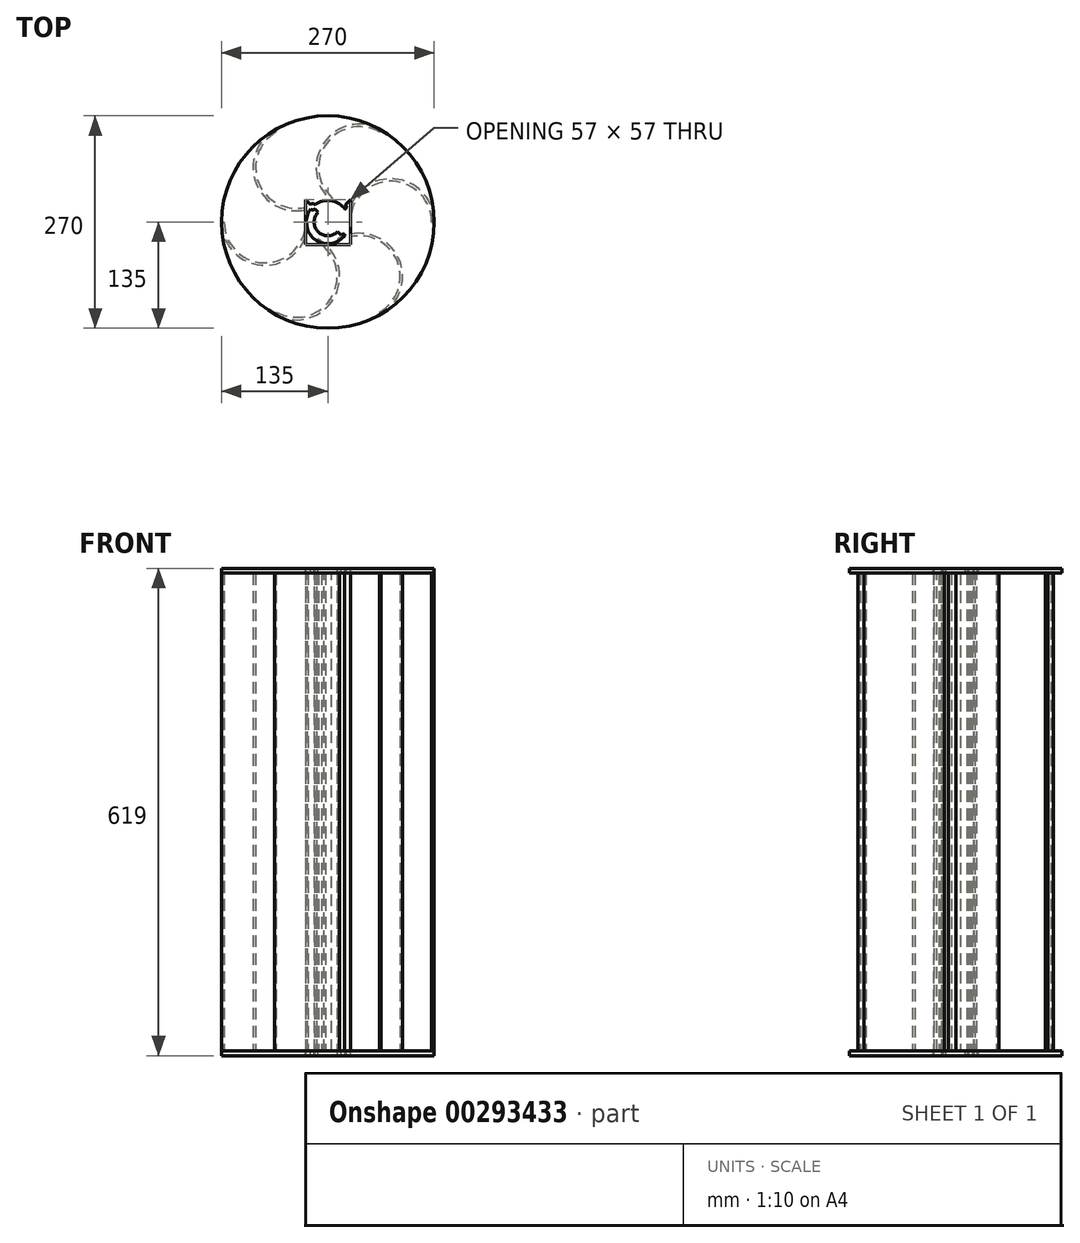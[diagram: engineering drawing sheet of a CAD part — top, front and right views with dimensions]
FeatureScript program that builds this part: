
annotation { "Feature Type Name" : "Feature", "Feature Type Description" : "" }
export const myFeature = defineFeature(function(context is Context, id is Id, definition is map)
    precondition{}
    {
        {
            var Q0;
            Q0=qCreatedBy(makeId("Top.planeOp"),FACE);
            var sketch = newSketch(context, id + "F0", { "sketchPlane" : qUnion([Q0])});
            skCircle(sketch, "E0", {"center": v(0, 0) * mm, "radius": 135 * mm});
            skSolve(sketch);
        }
        {
            var Q0;
            Q0 = qSketchRegion(id + "F0", true);
            extrude(context, id + "F1", {"entities" : qUnion([Q0]), "depth" : 6 * mm});
        }
        {
            var Q0;
            Q0=makeQuery(id+"F1.opExtrude","CAP_FACE",FACE,{"disambiguationData":[OSD([sQuery(id+"F0.wireOp",EDGE,"E0")])],"isStart":false});
            var sketch = newSketch(context, id + "F2", { "sketchPlane" : qUnion([Q0])});
            skCircle(sketch, "E1", {"center": v(0, 0) * mm, "radius": 80 * mm});
            skLineSegment(sketch, "E2", {"start": v(-67.5, 116.91) * mm, "end": v(67.5, -116.91) * mm});
            skLineSegment(sketch, "E3", {"start": v(-67.5, -116.91) * mm, "end": v(67.5, 116.91) * mm});
            skLineSegment(sketch, "E4", {"start": v(-135, 0) * mm, "end": v(135, 0) * mm});
            skArc(sketch, "E5", {"start": v(-131.8, 0) * mm, "mid": v(-80, -51.8) * mm, "end": v(-28.2, 0) * mm});
            skArc(sketch, "E6", {"start": v(-65.9, -114.14) * mm, "mid": v(4.86, -95.18) * mm, "end": v(-14.1, -24.42) * mm});
            skArc(sketch, "E7", {"start": v(65.9, -114.14) * mm, "mid": v(84.86, -43.38) * mm, "end": v(14.1, -24.42) * mm});
            skArc(sketch, "E8", {"start": v(131.8, 0) * mm, "mid": v(80, 51.8) * mm, "end": v(28.2, 0) * mm});
            skArc(sketch, "E9", {"start": v(65.9, 114.14) * mm, "mid": v(-4.86, 95.18) * mm, "end": v(14.1, 24.42) * mm});
            skArc(sketch, "E10", {"start": v(-65.9, 114.14) * mm, "mid": v(-84.86, 43.38) * mm, "end": v(-14.1, 24.42) * mm});
            skArc(sketch, "E11.0", {"start": v(-67.5, 116.91) * mm, "mid": v(-87.63, 41.78) * mm, "end": v(-12.5, 21.65) * mm});
            skArc(sketch, "E12.0", {"start": v(-135, 0) * mm, "mid": v(-80, -55) * mm, "end": v(-25, 0) * mm});
            skArc(sketch, "E13.0", {"start": v(-67.5, -116.91) * mm, "mid": v(7.63, -96.78) * mm, "end": v(-12.5, -21.65) * mm});
            skArc(sketch, "E14.0", {"start": v(67.5, -116.91) * mm, "mid": v(87.63, -41.78) * mm, "end": v(12.5, -21.65) * mm});
            skArc(sketch, "E15.0", {"start": v(135, 0) * mm, "mid": v(80, 55) * mm, "end": v(25, 0) * mm});
            skArc(sketch, "E16.0", {"start": v(67.5, 116.91) * mm, "mid": v(-7.63, 96.78) * mm, "end": v(12.5, 21.65) * mm});
            skSolve(sketch);
        }
        {
            var Q0;
            {var subQ0=sQuery(id+"F2.wireOp",EDGE,"E5");var subQ1=sQuery(id+"F2.wireOp",EDGE,"E1");var subQ2=makeQuery(id+"F2.imprint","INTERSECT",VERTEX,{"derivedFrom":[subQ1,subQ0]});Q0=makeQuery(id+"F2.imprint","IMPRINT",FACE,{"disambiguationData":[TD([[makeQuery(id+"F2.imprint","IMPRINT",EDGE,{"disambiguationData":[TD([[subQ2,-1.0]])],"derivedFrom":subQ1}),-1.0]])]});}
            var Q1;
            {var subQ0=sQuery(id+"F2.wireOp",EDGE,"E5");var subQ1=sQuery(id+"F2.wireOp",EDGE,"E1");var subQ2=makeQuery(id+"F2.imprint","INTERSECT",VERTEX,{"derivedFrom":[subQ1,subQ0]});Q1=makeQuery(id+"F2.imprint","IMPRINT",FACE,{"disambiguationData":[TD([[makeQuery(id+"F2.imprint","IMPRINT",EDGE,{"disambiguationData":[TD([[subQ2,-1.0]])],"derivedFrom":subQ1}),1.0]])]});}
            var Q2;
            {var subQ0=sQuery(id+"F2.wireOp",EDGE,"E6");var subQ1=sQuery(id+"F2.wireOp",EDGE,"E1");var subQ2=makeQuery(id+"F2.imprint","INTERSECT",VERTEX,{"derivedFrom":[subQ1,subQ0]});Q2=makeQuery(id+"F2.imprint","IMPRINT",FACE,{"disambiguationData":[TD([[makeQuery(id+"F2.imprint","IMPRINT",EDGE,{"disambiguationData":[TD([[subQ2,-1.0]])],"derivedFrom":subQ1}),1.0]])]});}
            var Q3;
            {var subQ0=sQuery(id+"F2.wireOp",EDGE,"E6");var subQ1=sQuery(id+"F2.wireOp",EDGE,"E1");var subQ2=makeQuery(id+"F2.imprint","INTERSECT",VERTEX,{"derivedFrom":[subQ1,subQ0]});Q3=makeQuery(id+"F2.imprint","IMPRINT",FACE,{"disambiguationData":[TD([[makeQuery(id+"F2.imprint","IMPRINT",EDGE,{"disambiguationData":[TD([[subQ2,-1.0]])],"derivedFrom":subQ1}),-1.0]])]});}
            var Q4;
            {var subQ0=sQuery(id+"F2.wireOp",EDGE,"E10");var subQ1=sQuery(id+"F2.wireOp",EDGE,"E1");var subQ2=makeQuery(id+"F2.imprint","INTERSECT",VERTEX,{"derivedFrom":[subQ1,subQ0]});Q4=makeQuery(id+"F2.imprint","IMPRINT",FACE,{"disambiguationData":[TD([[makeQuery(id+"F2.imprint","IMPRINT",EDGE,{"disambiguationData":[TD([[subQ2,-1.0]])],"derivedFrom":subQ1}),1.0]])]});}
            var Q5;
            {var subQ0=sQuery(id+"F2.wireOp",EDGE,"E10");var subQ1=sQuery(id+"F2.wireOp",EDGE,"E1");var subQ2=makeQuery(id+"F2.imprint","INTERSECT",VERTEX,{"derivedFrom":[subQ1,subQ0]});Q5=makeQuery(id+"F2.imprint","IMPRINT",FACE,{"disambiguationData":[TD([[makeQuery(id+"F2.imprint","IMPRINT",EDGE,{"disambiguationData":[TD([[subQ2,-1.0]])],"derivedFrom":subQ1}),-1.0]])]});}
            var Q6;
            {var subQ0=sQuery(id+"F2.wireOp",EDGE,"E9");var subQ1=sQuery(id+"F2.wireOp",EDGE,"E1");var subQ2=makeQuery(id+"F2.imprint","INTERSECT",VERTEX,{"derivedFrom":[subQ1,subQ0]});Q6=makeQuery(id+"F2.imprint","IMPRINT",FACE,{"disambiguationData":[TD([[makeQuery(id+"F2.imprint","IMPRINT",EDGE,{"disambiguationData":[TD([[subQ2,-1.0]])],"derivedFrom":subQ1}),-1.0]])]});}
            var Q7;
            {var subQ0=sQuery(id+"F2.wireOp",EDGE,"E9");var subQ1=sQuery(id+"F2.wireOp",EDGE,"E1");var subQ2=makeQuery(id+"F2.imprint","INTERSECT",VERTEX,{"derivedFrom":[subQ1,subQ0]});Q7=makeQuery(id+"F2.imprint","IMPRINT",FACE,{"disambiguationData":[TD([[makeQuery(id+"F2.imprint","IMPRINT",EDGE,{"disambiguationData":[TD([[subQ2,-1.0]])],"derivedFrom":subQ1}),1.0]])]});}
            var Q8;
            {var subQ0=sQuery(id+"F2.wireOp",EDGE,"E8");var subQ1=sQuery(id+"F2.wireOp",EDGE,"E1");var subQ2=makeQuery(id+"F2.imprint","INTERSECT",VERTEX,{"derivedFrom":[subQ1,subQ0]});Q8=makeQuery(id+"F2.imprint","IMPRINT",FACE,{"disambiguationData":[TD([[makeQuery(id+"F2.imprint","IMPRINT",EDGE,{"disambiguationData":[TD([[subQ2,-1.0]])],"derivedFrom":subQ1}),1.0]])]});}
            var Q9;
            {var subQ0=sQuery(id+"F2.wireOp",EDGE,"E7");var subQ1=sQuery(id+"F2.wireOp",EDGE,"E1");var subQ2=makeQuery(id+"F2.imprint","INTERSECT",VERTEX,{"derivedFrom":[subQ1,subQ0]});Q9=makeQuery(id+"F2.imprint","IMPRINT",FACE,{"disambiguationData":[TD([[makeQuery(id+"F2.imprint","IMPRINT",EDGE,{"disambiguationData":[TD([[subQ2,-1.0]])],"derivedFrom":subQ1}),1.0]])]});}
            var Q10;
            {var subQ0=sQuery(id+"F2.wireOp",EDGE,"E7");var subQ1=sQuery(id+"F2.wireOp",EDGE,"E1");var subQ2=makeQuery(id+"F2.imprint","INTERSECT",VERTEX,{"derivedFrom":[subQ1,subQ0]});Q10=makeQuery(id+"F2.imprint","IMPRINT",FACE,{"disambiguationData":[TD([[makeQuery(id+"F2.imprint","IMPRINT",EDGE,{"disambiguationData":[TD([[subQ2,-1.0]])],"derivedFrom":subQ1}),-1.0]])]});}
            var Q11;
            {var subQ0=sQuery(id+"F2.wireOp",EDGE,"E8");var subQ1=sQuery(id+"F2.wireOp",EDGE,"E1");var subQ2=makeQuery(id+"F2.imprint","INTERSECT",VERTEX,{"derivedFrom":[subQ1,subQ0]});Q11=makeQuery(id+"F2.imprint","IMPRINT",FACE,{"disambiguationData":[TD([[makeQuery(id+"F2.imprint","IMPRINT",EDGE,{"disambiguationData":[TD([[subQ2,-1.0]])],"derivedFrom":subQ1}),-1.0]])]});}
            extrude(context, id + "F3", {"entities" : qUnion([Q0, Q1, Q2, Q3, Q4, Q5, Q6, Q7, Q8, Q9, Q10, Q11]), "operationType" : NewBodyOperationType.ADD, "depth" : 607 * mm, "offsetDistance" : 25 * mm});
        }
        {
            var Q0;
            Q0=makeQuery(id+"F3.opExtrude","CAP_FACE",FACE,{"disambiguationData":[OSD([sQuery(id+"F2.wireOp",EDGE,"E2"),sQuery(id+"F2.wireOp",EDGE,"E10"),sQuery(id+"F2.wireOp",EDGE,"E11.0")])],"isStart":false});
            var sketch = newSketch(context, id + "F4", { "sketchPlane" : qUnion([Q0])});
            skCircle(sketch, "E17", {"center": v(0, 0) * mm, "radius": 135 * mm});
            skSolve(sketch);
        }
        {
            var Q0;
            Q0 = qSketchRegion(id + "F4", true);
            extrude(context, id + "F5", {"entities" : qUnion([Q0]), "operationType" : NewBodyOperationType.ADD, "depth" : 6 * mm});
        }
        {
            var Q0;
            Q0=makeQuery(id+"F5.opExtrude","CAP_FACE",FACE,{"disambiguationData":[OSD([sQuery(id+"F4.wireOp",EDGE,"E17")])],"isStart":false});
            var sketch = newSketch(context, id + "F6", { "sketchPlane" : qUnion([Q0])});
            skCircle(sketch, "E18", {"center": v(0, 0) * mm, "radius": 17.5 * mm});
            skLineSegment(sketch, "E19.bottom", {"start": v(28.5, 28.5) * mm, "end": v(-28.5, 28.5) * mm});
            skLineSegment(sketch, "E19.top", {"start": v(28.5, -28.5) * mm, "end": v(-28.5, -28.5) * mm});
            skLineSegment(sketch, "E19.left", {"start": v(28.5, 28.5) * mm, "end": v(28.5, -28.5) * mm});
            skLineSegment(sketch, "E19.right", {"start": v(-28.5, 28.5) * mm, "end": v(-28.5, -28.5) * mm});
            skLineSegment(sketch, "E20", {"start": v(-28.5, 28.5) * mm, "end": v(28.5, -28.5) * mm});
            skLineSegment(sketch, "E21", {"start": v(28.5, 28.5) * mm, "end": v(-28.5, -28.5) * mm});
            skCircle(sketch, "E22", {"center": v(0, 0) * mm, "radius": 27.5 * mm});
            skCircle(sketch, "E23", {"center": v(-19.45, 19.45) * mm, "radius": 4 * mm});
            skCircle(sketch, "E24", {"center": v(-19.45, -19.45) * mm, "radius": 4 * mm});
            skCircle(sketch, "E25", {"center": v(19.45, -19.45) * mm, "radius": 4 * mm});
            skCircle(sketch, "E26", {"center": v(19.45, 19.45) * mm, "radius": 4 * mm});
            skSolve(sketch);
        }
        {
            var Q0;
            {var subQ0=sQuery(id+"F6.wireOp",EDGE,"E23");var subQ1=sQuery(id+"F6.wireOp",EDGE,"E20");var subQ2=makeQuery(id+"F6.imprint","INTERSECT",VERTEX,{"disambiguationData":[OD(0.0)],"derivedFrom":[subQ1,subQ0]});Q0=makeQuery(id+"F6.imprint","IMPRINT",FACE,{"disambiguationData":[TD([[makeQuery(id+"F6.imprint","IMPRINT",EDGE,{"disambiguationData":[TD([[subQ2,-1.0]])],"derivedFrom":subQ1}),1.0]])]});}
            var Q1;
            {var subQ0=sQuery(id+"F6.wireOp",EDGE,"E23");var subQ1=sQuery(id+"F6.wireOp",EDGE,"E20");var subQ2=makeQuery(id+"F6.imprint","INTERSECT",VERTEX,{"disambiguationData":[OD(0.0)],"derivedFrom":[subQ1,subQ0]});Q1=makeQuery(id+"F6.imprint","IMPRINT",FACE,{"disambiguationData":[TD([[makeQuery(id+"F6.imprint","IMPRINT",EDGE,{"disambiguationData":[TD([[subQ2,-1.0]])],"derivedFrom":subQ1}),-1.0]])]});}
            var Q2;
            {var subQ0=sQuery(id+"F6.wireOp",EDGE,"E22");var subQ1=sQuery(id+"F6.wireOp",EDGE,"E20");var subQ2=makeQuery(id+"F6.imprint","INTERSECT",VERTEX,{"disambiguationData":[OD(0.0)],"derivedFrom":[subQ1,subQ0]});Q2=makeQuery(id+"F6.imprint","IMPRINT",FACE,{"disambiguationData":[TD([[makeQuery(id+"F6.imprint","IMPRINT",EDGE,{"disambiguationData":[TD([[subQ2,-1.0]])],"derivedFrom":subQ1}),-1.0]])]});}
            var Q3;
            {var subQ0=sQuery(id+"F6.wireOp",EDGE,"E22");var subQ1=sQuery(id+"F6.wireOp",EDGE,"E20");var subQ2=makeQuery(id+"F6.imprint","INTERSECT",VERTEX,{"disambiguationData":[OD(0.0)],"derivedFrom":[subQ1,subQ0]});Q3=makeQuery(id+"F6.imprint","IMPRINT",FACE,{"disambiguationData":[TD([[makeQuery(id+"F6.imprint","IMPRINT",EDGE,{"disambiguationData":[TD([[subQ2,-1.0]])],"derivedFrom":subQ1}),1.0]])]});}
            var Q4;
            {var subQ0=sQuery(id+"F6.wireOp",EDGE,"E20");var subQ1=sQuery(id+"F6.wireOp",EDGE,"E18");var subQ2=makeQuery(id+"F6.imprint","INTERSECT",VERTEX,{"disambiguationData":[OD(0.0)],"derivedFrom":[subQ1,subQ0]});Q4=makeQuery(id+"F6.imprint","IMPRINT",FACE,{"disambiguationData":[TD([[makeQuery(id+"F6.imprint","IMPRINT",EDGE,{"disambiguationData":[TD([[subQ2,-1.0]])],"derivedFrom":subQ1}),1.0]])]});}
            var Q5;
            {var subQ0=sQuery(id+"F6.wireOp",EDGE,"E21");var subQ1=sQuery(id+"F6.wireOp",EDGE,"E18");var subQ2=makeQuery(id+"F6.imprint","INTERSECT",VERTEX,{"disambiguationData":[OD(1.0)],"derivedFrom":[subQ1,subQ0]});Q5=makeQuery(id+"F6.imprint","IMPRINT",FACE,{"disambiguationData":[TD([[makeQuery(id+"F6.imprint","IMPRINT",EDGE,{"disambiguationData":[TD([[subQ2,-1.0]])],"derivedFrom":subQ1}),1.0]])]});}
            var Q6;
            {var subQ0=sQuery(id+"F6.wireOp",EDGE,"E21");var subQ1=sQuery(id+"F6.wireOp",EDGE,"E18");var subQ2=makeQuery(id+"F6.imprint","INTERSECT",VERTEX,{"disambiguationData":[OD(0.0)],"derivedFrom":[subQ1,subQ0]});Q6=makeQuery(id+"F6.imprint","IMPRINT",FACE,{"disambiguationData":[TD([[makeQuery(id+"F6.imprint","IMPRINT",EDGE,{"disambiguationData":[TD([[subQ2,1.0]])],"derivedFrom":subQ1}),1.0]])]});}
            var Q7;
            {var subQ0=sQuery(id+"F6.wireOp",EDGE,"E20");var subQ1=sQuery(id+"F6.wireOp",EDGE,"E18");var subQ2=makeQuery(id+"F6.imprint","INTERSECT",VERTEX,{"disambiguationData":[OD(0.0)],"derivedFrom":[subQ1,subQ0]});Q7=makeQuery(id+"F6.imprint","IMPRINT",FACE,{"disambiguationData":[TD([[makeQuery(id+"F6.imprint","IMPRINT",EDGE,{"disambiguationData":[TD([[subQ2,1.0]])],"derivedFrom":subQ1}),1.0]])]});}
            var Q8;
            {var subQ0=sQuery(id+"F6.wireOp",EDGE,"E26");var subQ1=sQuery(id+"F6.wireOp",EDGE,"E21");var subQ2=makeQuery(id+"F6.imprint","INTERSECT",VERTEX,{"disambiguationData":[OD(0.0)],"derivedFrom":[subQ1,subQ0]});Q8=makeQuery(id+"F6.imprint","IMPRINT",FACE,{"disambiguationData":[TD([[makeQuery(id+"F6.imprint","IMPRINT",EDGE,{"disambiguationData":[TD([[subQ2,-1.0]])],"derivedFrom":subQ1}),1.0]])]});}
            var Q9;
            {var subQ0=sQuery(id+"F6.wireOp",EDGE,"E26");var subQ1=sQuery(id+"F6.wireOp",EDGE,"E21");var subQ2=makeQuery(id+"F6.imprint","INTERSECT",VERTEX,{"disambiguationData":[OD(0.0)],"derivedFrom":[subQ1,subQ0]});Q9=makeQuery(id+"F6.imprint","IMPRINT",FACE,{"disambiguationData":[TD([[makeQuery(id+"F6.imprint","IMPRINT",EDGE,{"disambiguationData":[TD([[subQ2,-1.0]])],"derivedFrom":subQ1}),-1.0]])]});}
            var Q10;
            {var subQ0=sQuery(id+"F6.wireOp",EDGE,"E22");var subQ1=sQuery(id+"F6.wireOp",EDGE,"E21");var subQ2=makeQuery(id+"F6.imprint","INTERSECT",VERTEX,{"disambiguationData":[OD(0.0)],"derivedFrom":[subQ1,subQ0]});Q10=makeQuery(id+"F6.imprint","IMPRINT",FACE,{"disambiguationData":[TD([[makeQuery(id+"F6.imprint","IMPRINT",EDGE,{"disambiguationData":[TD([[subQ2,-1.0]])],"derivedFrom":subQ1}),-1.0]])]});}
            var Q11;
            {var subQ0=sQuery(id+"F6.wireOp",EDGE,"E22");var subQ1=sQuery(id+"F6.wireOp",EDGE,"E21");var subQ2=makeQuery(id+"F6.imprint","INTERSECT",VERTEX,{"disambiguationData":[OD(0.0)],"derivedFrom":[subQ1,subQ0]});Q11=makeQuery(id+"F6.imprint","IMPRINT",FACE,{"disambiguationData":[TD([[makeQuery(id+"F6.imprint","IMPRINT",EDGE,{"disambiguationData":[TD([[subQ2,-1.0]])],"derivedFrom":subQ1}),1.0]])]});}
            var Q12;
            {var subQ0=sQuery(id+"F6.wireOp",EDGE,"E22");var subQ1=sQuery(id+"F6.wireOp",EDGE,"E20");var subQ2=makeQuery(id+"F6.imprint","INTERSECT",VERTEX,{"disambiguationData":[OD(1.0)],"derivedFrom":[subQ1,subQ0]});Q12=makeQuery(id+"F6.imprint","IMPRINT",FACE,{"disambiguationData":[TD([[makeQuery(id+"F6.imprint","IMPRINT",EDGE,{"disambiguationData":[TD([[subQ2,-1.0]])],"derivedFrom":subQ1}),-1.0]])]});}
            var Q13;
            {var subQ0=sQuery(id+"F6.wireOp",EDGE,"E22");var subQ1=sQuery(id+"F6.wireOp",EDGE,"E20");var subQ2=makeQuery(id+"F6.imprint","INTERSECT",VERTEX,{"disambiguationData":[OD(1.0)],"derivedFrom":[subQ1,subQ0]});Q13=makeQuery(id+"F6.imprint","IMPRINT",FACE,{"disambiguationData":[TD([[makeQuery(id+"F6.imprint","IMPRINT",EDGE,{"disambiguationData":[TD([[subQ2,-1.0]])],"derivedFrom":subQ1}),1.0]])]});}
            var Q14;
            {var subQ0=sQuery(id+"F6.wireOp",EDGE,"E25");var subQ1=sQuery(id+"F6.wireOp",EDGE,"E20");var subQ2=makeQuery(id+"F6.imprint","INTERSECT",VERTEX,{"disambiguationData":[OD(0.0)],"derivedFrom":[subQ1,subQ0]});Q14=makeQuery(id+"F6.imprint","IMPRINT",FACE,{"disambiguationData":[TD([[makeQuery(id+"F6.imprint","IMPRINT",EDGE,{"disambiguationData":[TD([[subQ2,-1.0]])],"derivedFrom":subQ1}),1.0]])]});}
            var Q15;
            {var subQ0=sQuery(id+"F6.wireOp",EDGE,"E25");var subQ1=sQuery(id+"F6.wireOp",EDGE,"E20");var subQ2=makeQuery(id+"F6.imprint","INTERSECT",VERTEX,{"disambiguationData":[OD(0.0)],"derivedFrom":[subQ1,subQ0]});Q15=makeQuery(id+"F6.imprint","IMPRINT",FACE,{"disambiguationData":[TD([[makeQuery(id+"F6.imprint","IMPRINT",EDGE,{"disambiguationData":[TD([[subQ2,-1.0]])],"derivedFrom":subQ1}),-1.0]])]});}
            var Q16;
            {var subQ0=sQuery(id+"F6.wireOp",EDGE,"E22");var subQ1=sQuery(id+"F6.wireOp",EDGE,"E21");var subQ2=makeQuery(id+"F6.imprint","INTERSECT",VERTEX,{"disambiguationData":[OD(1.0)],"derivedFrom":[subQ1,subQ0]});Q16=makeQuery(id+"F6.imprint","IMPRINT",FACE,{"disambiguationData":[TD([[makeQuery(id+"F6.imprint","IMPRINT",EDGE,{"disambiguationData":[TD([[subQ2,-1.0]])],"derivedFrom":subQ1}),1.0]])]});}
            var Q17;
            {var subQ0=sQuery(id+"F6.wireOp",EDGE,"E22");var subQ1=sQuery(id+"F6.wireOp",EDGE,"E21");var subQ2=makeQuery(id+"F6.imprint","INTERSECT",VERTEX,{"disambiguationData":[OD(1.0)],"derivedFrom":[subQ1,subQ0]});Q17=makeQuery(id+"F6.imprint","IMPRINT",FACE,{"disambiguationData":[TD([[makeQuery(id+"F6.imprint","IMPRINT",EDGE,{"disambiguationData":[TD([[subQ2,-1.0]])],"derivedFrom":subQ1}),-1.0]])]});}
            var Q18;
            {var subQ0=sQuery(id+"F6.wireOp",EDGE,"E24");var subQ1=sQuery(id+"F6.wireOp",EDGE,"E21");var subQ2=makeQuery(id+"F6.imprint","INTERSECT",VERTEX,{"disambiguationData":[OD(0.0)],"derivedFrom":[subQ1,subQ0]});Q18=makeQuery(id+"F6.imprint","IMPRINT",FACE,{"disambiguationData":[TD([[makeQuery(id+"F6.imprint","IMPRINT",EDGE,{"disambiguationData":[TD([[subQ2,-1.0]])],"derivedFrom":subQ1}),-1.0]])]});}
            var Q19;
            {var subQ0=sQuery(id+"F6.wireOp",EDGE,"E24");var subQ1=sQuery(id+"F6.wireOp",EDGE,"E21");var subQ2=makeQuery(id+"F6.imprint","INTERSECT",VERTEX,{"disambiguationData":[OD(0.0)],"derivedFrom":[subQ1,subQ0]});Q19=makeQuery(id+"F6.imprint","IMPRINT",FACE,{"disambiguationData":[TD([[makeQuery(id+"F6.imprint","IMPRINT",EDGE,{"disambiguationData":[TD([[subQ2,-1.0]])],"derivedFrom":subQ1}),1.0]])]});}
            extrude(context, id + "F7", {"entities" : qUnion([Q0, Q1, Q2, Q3, Q4, Q5, Q6, Q7, Q8, Q9, Q10, Q11, Q12, Q13, Q14, Q15, Q16, Q17, Q18, Q19]), "operationType" : NewBodyOperationType.REMOVE, "endBound" : BoundingType.THROUGH_ALL, "oppositeDirection" : true, "depth" : 25 * mm});
        }
    });
